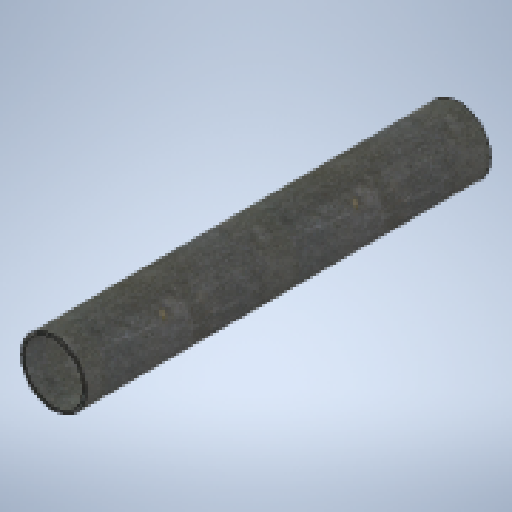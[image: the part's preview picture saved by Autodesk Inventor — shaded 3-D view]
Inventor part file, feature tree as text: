
AUTODESK INVENTOR PART (.ipt)
format: ipt  version: 2025.1 (Build 291241020, 241B)  size: 150,528 bytes
history: native  units: mm
features: extrude x1, sketch x1
ambient origin geometry x8: Origin, YZ Plane, XZ Plane, XY Plane, X Axis, Y Axis, Z Axis, Center Point
bodies: Solid1 (feature_tree)
feature tree (2):
  extrude  "Extrusion1"  Depth=370.0mm
  sketch  "Sketch1"  dims[d0=60.0mm d1=3.0mm d2=370.0mm d3=0.0mm]
